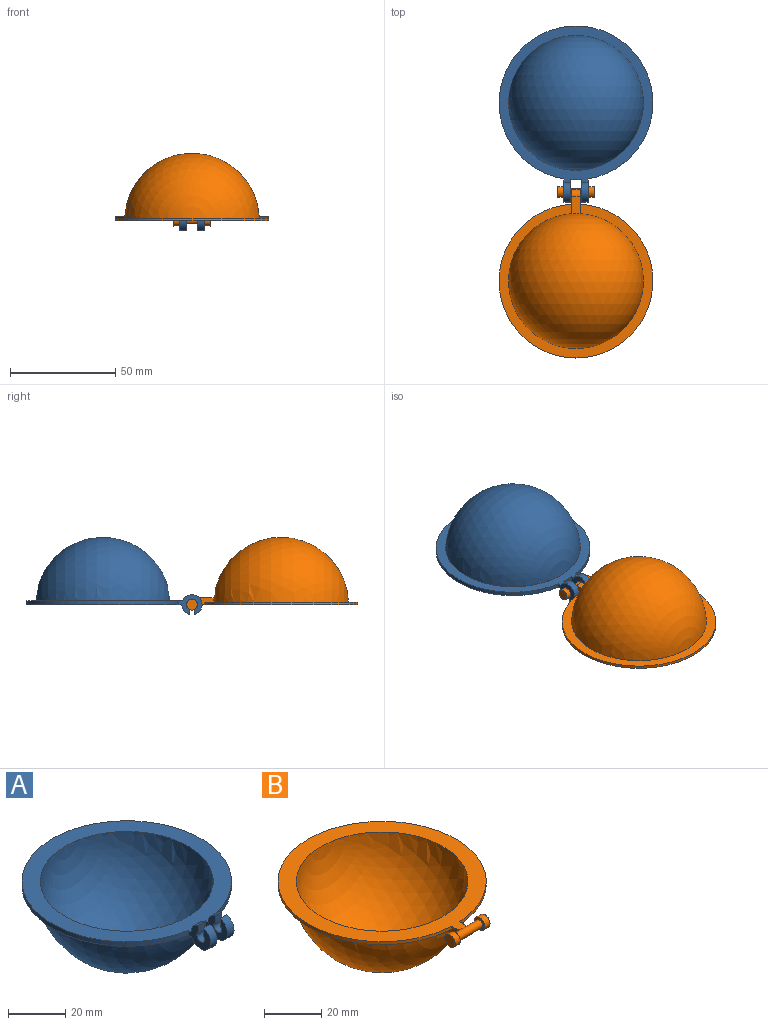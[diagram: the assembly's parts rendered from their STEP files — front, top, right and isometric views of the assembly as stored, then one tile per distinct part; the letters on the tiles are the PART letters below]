
ASSEMBLY  parts=2 mates=1
PART A: 20 faces, bbox 73x83.5x42.8 mm
  f0: cylinder r=4.8mm len=4.64mm, axis (1,0,0), area 20.1mm2, adj f4,f10,f11,f18
  f1: cylinder r=4.8mm len=4.64mm, axis (-1,0,0), area 20.1mm2, adj f2,f3,f4,f16
  f2: plane 11.02x9.44mm, normal (-1,0,0), area 56.3mm2, adj f1,f4,f5,f8,f14,f15,f16,f17
  f3: plane 10.65x9.44mm, normal (1,0,0), area 55.6mm2, adj f1,f4,f5,f6,f14,f15,f16,f17
  f4: plane 73.92x72.96mm, normal (0,0,1), area 1346mm2, adj f0,f1,f2,f3,f6,f7,f8,f10
  f5: plane 74.32x72.96mm, normal (0,0,-1), area 985.7mm2, adj f2,f3,f6,f8,f9,f10,f11,f13
  f6: cylinder r=36.48mm len=5.12mm, axis (0,0,1), area 9.8mm2, adj f3,f4,f5,f11
  f7: sphere r=30.08mm, area 5685.1mm2, adj f4
  f8: cylinder r=36.48mm len=72.96mm, axis (0,0,1), area 417.9mm2, adj f2,f4,f5,f10
  f9: sphere r=32mm, area 6049.4mm2, adj f5
  f10: plane 11.02x9.44mm, normal (1,0,0), area 56.3mm2, adj f0,f4,f5,f8,f12,f13,f18,f19
  f11: plane 10.65x9.44mm, normal (-1,0,0), area 55.6mm2, adj f0,f4,f5,f6,f12,f13,f18,f19
  f12: cylinder r=1.92mm len=3.84mm, axis (1,0,0), area 29.9mm2, adj f10,f11,f18,f19
  f13: cylinder r=4.8mm len=9.43mm, axis (1,0,0), area 62mm2, adj f5,f10,f11,f19
  f14: cylinder r=1.92mm len=3.84mm, axis (-1,0,0), area 29.9mm2, adj f2,f3,f16,f17
  f15: cylinder r=4.8mm len=9.43mm, axis (-1,0,0), area 62mm2, adj f2,f3,f5,f17
  f16: plane 3.2x3.17mm, normal (0,-1,0), area 10.1mm2, adj f1,f2,f3,f14
  f17: plane 3.2x3.18mm, normal (0,1,0), area 10.2mm2, adj f2,f3,f14,f15
  f18: plane 3.2x3.17mm, normal (0,-1,0), area 10.1mm2, adj f0,f10,f11,f12
  f19: plane 3.2x3.18mm, normal (0,1,0), area 10.2mm2, adj f10,f11,f12,f13
PART B: 16 faces, bbox 73x81.3x38.9 mm
  f0: plane 77.12x72.96mm, normal (0,0,1), area 1354.3mm2, adj f2,f3,f5,f6,f7
  f1: plane 72.96x72.91mm, normal (0,0,-1), area 951.6mm2, adj f3,f4,f5,f6
  f2: sphere r=30.08mm, area 5685.1mm2, adj f0
  f3: cylinder r=36.48mm len=72.96mm, axis (0,0,1), area 288.5mm2, adj f0,f1,f5,f6
  f4: sphere r=32mm, area 6157.8mm2, adj f1,f5,f6,f14
  f5: plane 11.42x3.2mm, normal (1,0,0), area 25.4mm2, adj f0,f1,f3,f4,f7,f14,f15
  f6: plane 11.42x3.2mm, normal (-1,0,0), area 25.4mm2, adj f0,f1,f3,f4,f7,f14,f15
  f7: cylinder r=1.6mm len=12.16mm, axis (-1,0,0), area 108.6mm2, adj f0,f5,f6,f10,f13,f15
  f8: cylinder r=2.56mm len=5.12mm, axis (-1,0,0), area 41.2mm2, adj f9,f10
  f9: plane 5.12x5.12mm, normal (1,0,0), area 20.6mm2, adj f8
  f10: plane 5.12x5.12mm, normal (-1,0,0), area 12.5mm2, adj f7,f8
  f11: cylinder r=2.56mm len=5.12mm, axis (1,0,0), area 41.2mm2, adj f12,f13
  f12: plane 5.12x5.12mm, normal (-1,0,0), area 20.6mm2, adj f11
  f13: plane 5.12x5.12mm, normal (1,0,0), area 12.5mm2, adj f7,f11
  f14: plane 8.49x3.84mm, normal (0,0,-1), area 32.4mm2, adj f4,f5,f6,f15
  f15: cylinder r=3.2mm len=3.84mm, axis (-1,0,0), area 14.2mm2, adj f5,f6,f7,f14
PLACE A rot(axis=(0,1,0),180deg) t=(28.91,24.96,24.98)mm
PLACE B rot(axis=(1,0,0),180deg) t=(28.89,-59.52,24.98)mm
MATE revolute A.f0 <-> B.f7  axis (1,0,0) through (34.67,-17.28,24.98)mm
